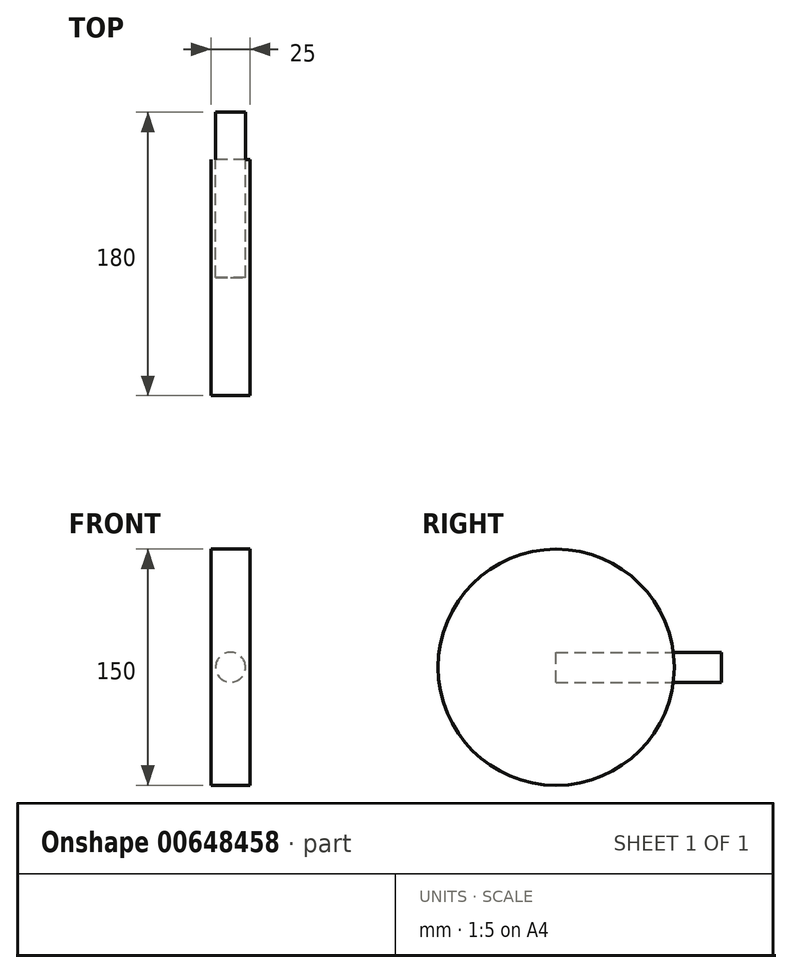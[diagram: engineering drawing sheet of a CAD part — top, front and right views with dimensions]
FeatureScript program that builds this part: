
annotation { "Feature Type Name" : "Feature", "Feature Type Description" : "" }
export const myFeature = defineFeature(function(context is Context, id is Id, definition is map)
    precondition{}
    {
        {
            var Q0;
            Q0=qCreatedBy(makeId("Front.planeOp"),FACE);
            var sketch = newSketch(context, id + "F0", { "sketchPlane" : qUnion([Q0])});
            skCircle(sketch, "E0", {"center": v(0, 0) * mm, "radius": 9.5 * mm});
            skSolve(sketch);
        }
        {
            var Q0;
            Q0=makeQuery(id+"F0.imprint","IMPRINT",FACE,{"disambiguationData":[TD([[makeQuery(id+"F0.imprint","IMPRINT",EDGE,{"derivedFrom":sQuery(id+"F0.wireOp",EDGE,"E0")}),1.0]])]});
            extrude(context, id + "F1", {"entities" : qUnion([Q0]), "depth" : 105 * mm, "offsetDistance" : 25 * mm});
        }
        {
            var Q0;
            Q0=qCreatedBy(makeId("Right.planeOp"),FACE);
            var sketch = newSketch(context, id + "F2", { "sketchPlane" : qUnion([Q0])});
            skCircle(sketch, "E1", {"center": v(-105, 0) * mm, "radius": 75 * mm});
            skSolve(sketch);
        }
        {
            var Q0;
            Q0=makeQuery(id+"F2.imprint","IMPRINT",FACE,{"disambiguationData":[TD([[makeQuery(id+"F2.imprint","IMPRINT",EDGE,{"derivedFrom":sQuery(id+"F2.wireOp",EDGE,"E1")}),1.0]])]});
            extrude(context, id + "F3", {"entities" : qUnion([Q0]), "endBound" : BoundingType.SYMMETRIC, "depth" : 25 * mm, "offsetDistance" : 25 * mm});
        }
    });
